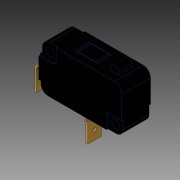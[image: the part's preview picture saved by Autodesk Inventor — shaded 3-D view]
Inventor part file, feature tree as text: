
AUTODESK INVENTOR PART (.ipt)
format: ipt  version: 2016 SP1 (Build 200210100, 210)  size: 244,736 bytes
history: native  units: in
note: dims shown in document units (in); Inventor stores cm internally (conversion verified against a paired STEP export)
features: extrude x3, sketch x3, mirror x2, plane x1, fillet x1
ambient origin geometry x8: Origin, YZ Plane, XZ Plane, XY Plane, X Axis, Y Axis, Z Axis, Center Point
bodies: Solid1 (feature_tree)
feature tree (10):
  extrude  "Extrusion1"  Depth=0.0197in
  plane  "Work Plane1"
  mirror  "Mirror1"
  extrude  "Extrusion2"  Depth=0.0472in
  mirror  "Mirror2"
  extrude  "Extrusion4"  Depth=0.0197in TaperAngle=0.0deg
  sketch  "Sketch1"  dims[d1=0.0197in d2=0.0in d5=0.0472in]
  sketch  "Sketch2"  dims[d6=0.0472in d7=0.0472in]
  sketch  "Sketch3"  dims[d8=0.0472in d9=0.0197in d10=0.0in d12=0.1969in d15=0.0079in d16=0.0079in d17=0.0394in d18=0.0197in d19=0.0in]
  fillet  "Fillet1"  Radius=0.1969in
